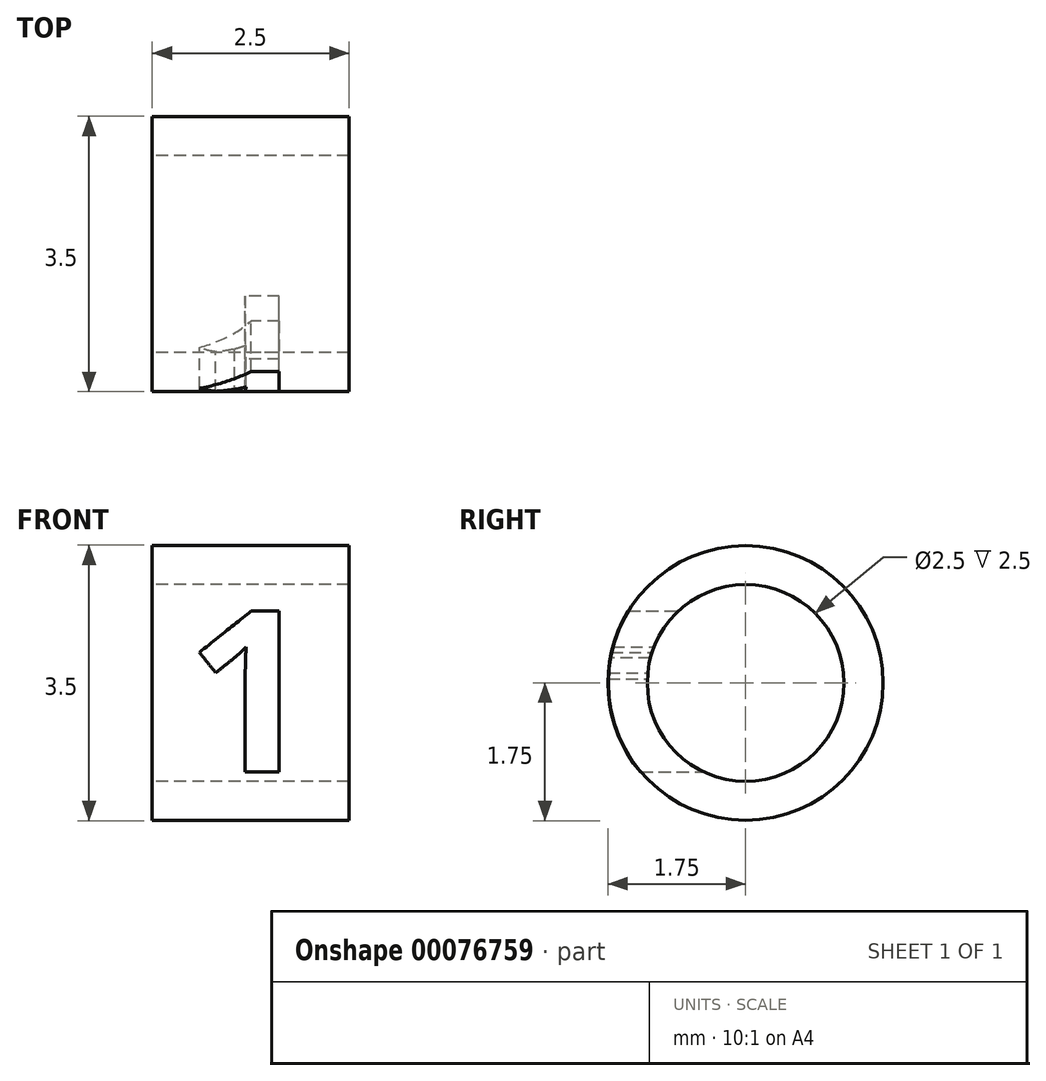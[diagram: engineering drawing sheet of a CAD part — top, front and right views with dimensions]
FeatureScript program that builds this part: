
annotation { "Feature Type Name" : "Feature", "Feature Type Description" : "" }
export const myFeature = defineFeature(function(context is Context, id is Id, definition is map)
    precondition{}
    {
        {
            var Q0;
            Q0=qCreatedBy(makeId("Right.planeOp"),FACE);
            var sketch = newSketch(context, id + "F0", { "sketchPlane" : qUnion([Q0])});
            skCircle(sketch, "E0", {"center": v(0, 0) * mm, "radius": 1.25 * mm});
            skCircle(sketch, "E1", {"center": v(0, 0) * mm, "radius": 1.75 * mm});
            skSolve(sketch);
        }
        {
            var Q0;
            Q0=makeQuery(id+"F0.imprint","IMPRINT",FACE,{"disambiguationData":[TD([[makeQuery(id+"F0.imprint","IMPRINT",EDGE,{"derivedFrom":sQuery(id+"F0.wireOp",EDGE,"E0")}),-1.0]])]});
            var Q1;
            Q1=makeQuery(id+"F0.imprint","IMPRINT",FACE,{"disambiguationData":[TD([[makeQuery(id+"F0.imprint","IMPRINT",EDGE,{"derivedFrom":sQuery(id+"F0.wireOp",EDGE,"E1")}),1.0]])]});
            extrude(context, id + "F1", {"entities" : qUnion([Q0, Q1]), "depth" : 2.5 * mm});
        }
        {
            var Q0;
            Q0=qCreatedBy(makeId("Front.planeOp"),FACE);
            var sketch = newSketch(context, id + "F2", { "sketchPlane" : qUnion([Q0])});
            skText(sketch, "E2", { "text": "1", "fontName": "OpenSans-Bold.ttf"});
            const initialGuessF2  = {"E2": [0.00043, -0.00113, 1, 0, 0.00206]};
            skSetInitialGuess(sketch, initialGuessF2);
            skSolve(sketch);
        }
        {
            var Q0;
            Q0=qSketchRegion(id+"F2",true);
            var Q1;
            Q1=qConstructionFilter(qBodyType(qCreatedBy(id+"F2",EDGE),BodyType.WIRE),ConstructionObject.NO);
            var Q2;
            Q2=makeQuery(id+"F1.opExtrude","SWEPT_FACE",FACE,{"disambiguationData":[OSD([sQuery(id+"F0.wireOp",EDGE,"E1")])]});
            var Q3;
            Q3=makeQuery(id+"F1.opExtrude","SWEPT_BODY",BODY,{"disambiguationData":[OSD([sQuery(id+"F0.wireOp",EDGE,"E0"),sQuery(id+"F0.wireOp",EDGE,"E1")])]});
            var Q4;
            Q4=sQuery(id+"F0.wireOp",VERTEX,"27635d6e-dcd6-4653-b727-4819003c0945");
            extrude(context, id + "F3", {"entities" : qUnion([Q0]), "operationType" : NewBodyOperationType.INTERSECT, "surfaceEntities" : qUnion([Q1]), "endBound" : BoundingType.UP_TO_SURFACE, "endBoundEntityFace" : qUnion([Q2]), "endBoundEntityBody" : qUnion([Q3]), "endBoundEntityVertex" : qUnion([Q4]), "depth" : 25 * mm});
        }
        {
            var Q0;
            Q0=makeQuery(id+"F0.imprint","IMPRINT",FACE,{"disambiguationData":[TD([[makeQuery(id+"F0.imprint","IMPRINT",EDGE,{"derivedFrom":sQuery(id+"F0.wireOp",EDGE,"E0")}),-1.0]])]});
            extrude(context, id + "F4", {"entities" : qUnion([Q0]), "depth" : 2.5 * mm});
        }
    });
